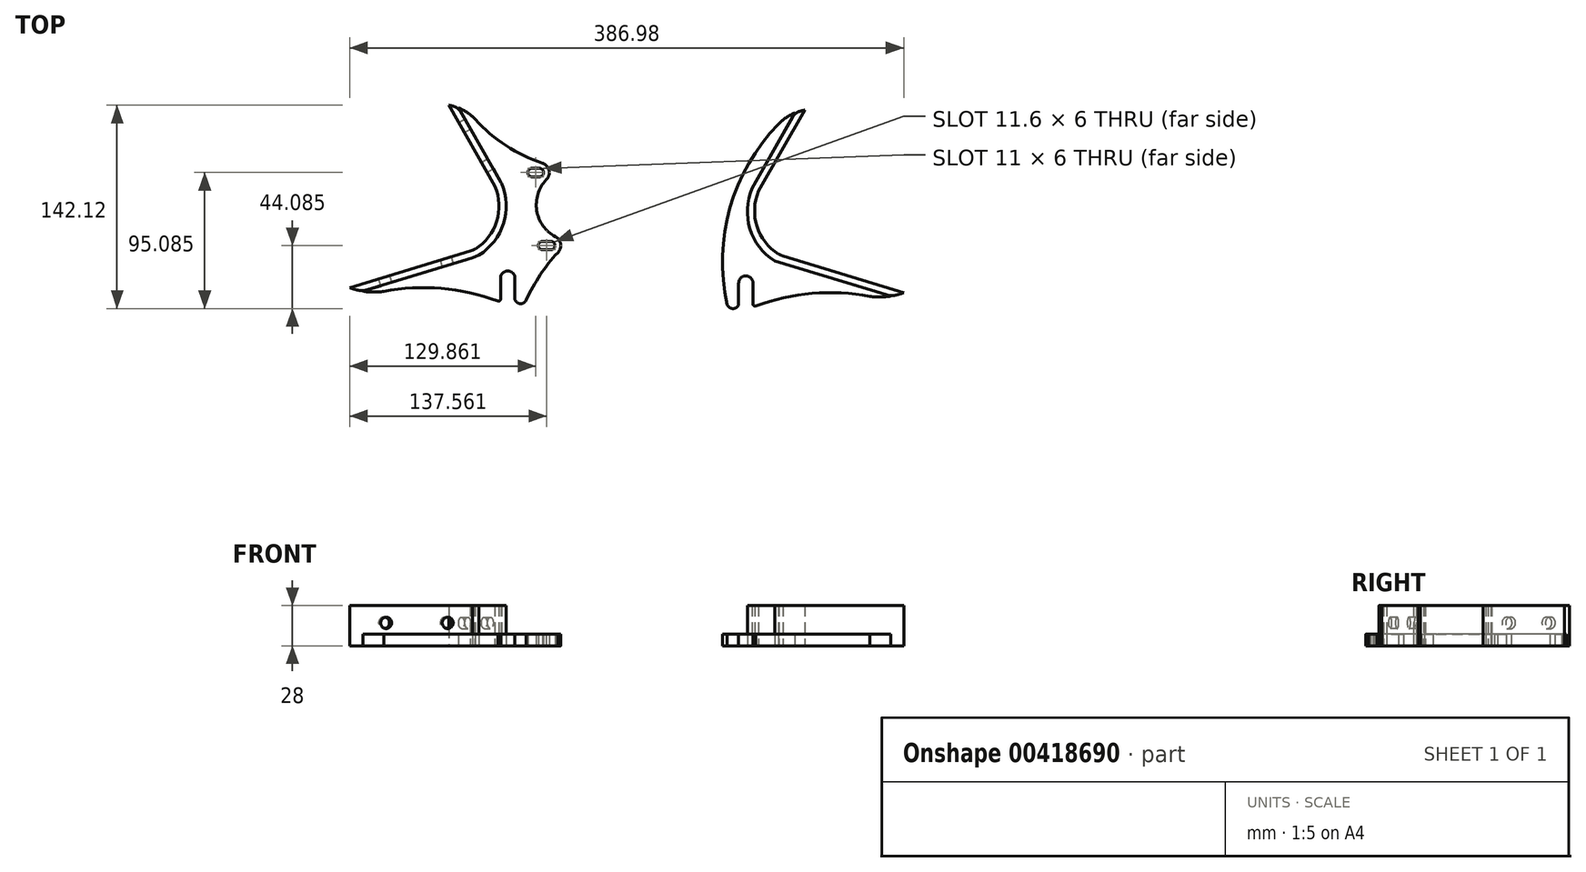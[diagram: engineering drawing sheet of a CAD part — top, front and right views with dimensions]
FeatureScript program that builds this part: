
annotation { "Feature Type Name" : "Feature", "Feature Type Description" : "" }
export const myFeature = defineFeature(function(context is Context, id is Id, definition is map)
    precondition{}
    {
        {
            var Q0;
            Q0=qCreatedBy(makeId("Top.planeOp"),FACE);
            var sketch = newSketch(context, id + "F0", { "sketchPlane" : qUnion([Q0])});
            skArc(sketch, "E0", {"start": v(92.06, 11.01) * mm, "mid": v(90.9, -13.55) * mm, "end": v(105.95, -33) * mm});
            skLineSegment(sketch, "E1", {"start": v(105.95, -33) * mm, "end": v(106.16, -33.11) * mm});
            skLineSegment(sketch, "E2", {"start": v(106.16, -33.11) * mm, "end": v(107.42, -33.6) * mm});
            skLineSegment(sketch, "E3", {"start": v(107.42, -33.6) * mm, "end": v(109.2, -34.29) * mm});
            skLineSegment(sketch, "E4", {"start": v(109.2, -34.29) * mm, "end": v(193.49, -59.91) * mm});
            skArc(sketch, "E5", {"start": v(88.13, -53.19) * mm, "mid": v(83.13, -48.19) * mm, "end": v(78.13, -53.19) * mm});
            skArc(sketch, "E6", {"start": v(88.13, -68.19) * mm, "mid": v(88.92, -69.1) * mm, "end": v(90.13, -69.19) * mm});
            skLineSegment(sketch, "E7", {"start": v(88.13, -53.19) * mm, "end": v(88.13, -68.19) * mm});
            skLineSegment(sketch, "E8", {"start": v(78.13, -53.19) * mm, "end": v(78.13, -68.19) * mm});
            skArc(sketch, "E9", {"start": v(70.13, -68.19) * mm, "mid": v(74.13, -71.06) * mm, "end": v(78.13, -68.19) * mm});
            skArc(sketch, "E10", {"start": v(169.82, -62.54) * mm, "mid": v(129.52, -60.4) * mm, "end": v(90.13, -69.19) * mm});
            skLineSegment(sketch, "E11", {"start": v(124.34, 67.6) * mm, "end": v(92.06, 11.01) * mm});
            skArc(sketch, "E12", {"start": v(105.82, 57.7) * mm, "mid": v(72.04, -0.73) * mm, "end": v(70.13, -68.19) * mm});
            skArc(sketch, "E13", {"start": v(-105.95, -29.54) * mm, "mid": v(-90.9, -10.09) * mm, "end": v(-92.06, 14.47) * mm});
            skLineSegment(sketch, "E14", {"start": v(-105.95, -29.54) * mm, "end": v(-106.16, -29.65) * mm});
            skLineSegment(sketch, "E15", {"start": v(-106.16, -29.65) * mm, "end": v(-107.42, -30.14) * mm});
            skLineSegment(sketch, "E16", {"start": v(-107.42, -30.14) * mm, "end": v(-109.2, -30.83) * mm});
            skLineSegment(sketch, "E17", {"start": v(-109.2, -30.83) * mm, "end": v(-193.49, -56.45) * mm});
            skArc(sketch, "E18", {"start": v(-103.3, -33.77) * mm, "mid": v(-86.14, -11.6) * mm, "end": v(-87.46, 16.42) * mm});
            skLineSegment(sketch, "E19", {"start": v(-107.75, -35.61) * mm, "end": v(-103.3, -33.77) * mm});
            skLineSegment(sketch, "E20", {"start": v(-87.72, 16.95) * mm, "end": v(-87.46, 16.42) * mm});
            skArc(sketch, "E21", {"start": v(-78.13, -49.73) * mm, "mid": v(-83.13, -44.73) * mm, "end": v(-88.13, -49.73) * mm});
            skArc(sketch, "E22", {"start": v(-90.13, -65.73) * mm, "mid": v(-88.92, -65.64) * mm, "end": v(-88.13, -64.73) * mm});
            skLineSegment(sketch, "E23", {"start": v(-88.13, -49.73) * mm, "end": v(-88.13, -64.73) * mm});
            skLineSegment(sketch, "E24", {"start": v(-78.13, -49.73) * mm, "end": v(-78.13, -64.73) * mm});
            skArc(sketch, "E25", {"start": v(-53.13, -29.98) * mm, "mid": v(-50.13, -26.98) * mm, "end": v(-53.13, -23.98) * mm});
            skArc(sketch, "E26", {"start": v(-61.13, 21.02) * mm, "mid": v(-58.13, 24.02) * mm, "end": v(-61.13, 27.02) * mm});
            skArc(sketch, "E27", {"start": v(-105.82, 61.16) * mm, "mid": v(-84.33, 42.8) * mm, "end": v(-58.82, 30.63) * mm});
            skArc(sketch, "E28", {"start": v(-58.73, -23.98) * mm, "mid": v(-60.85, -24.85) * mm, "end": v(-61.73, -26.98) * mm});
            skArc(sketch, "E29", {"start": v(-61.73, -26.98) * mm, "mid": v(-60.85, -29.1) * mm, "end": v(-58.73, -29.98) * mm});
            skLineSegment(sketch, "E30", {"start": v(-58.73, -29.98) * mm, "end": v(-53.13, -29.98) * mm});
            skLineSegment(sketch, "E31", {"start": v(-58.73, -23.98) * mm, "end": v(-53.13, -23.98) * mm});
            skArc(sketch, "E32", {"start": v(-66.13, 27.02) * mm, "mid": v(-68.25, 26.15) * mm, "end": v(-69.13, 24.02) * mm});
            skArc(sketch, "E33", {"start": v(-69.13, 24.02) * mm, "mid": v(-68.25, 21.9) * mm, "end": v(-66.13, 21.02) * mm});
            skLineSegment(sketch, "E34", {"start": v(-66.13, 21.02) * mm, "end": v(-61.13, 21.02) * mm});
            skLineSegment(sketch, "E35", {"start": v(-66.13, 27.02) * mm, "end": v(-61.13, 27.02) * mm});
            skArc(sketch, "E36", {"start": v(-56.34, 18.92) * mm, "mid": v(-62.84, -2.56) * mm, "end": v(-49.8, -20.82) * mm});
            skArc(sketch, "E37", {"start": v(-56.34, 18.92) * mm, "mid": v(-54.31, 25.62) * mm, "end": v(-59.1, 30.72) * mm});
            skArc(sketch, "E38", {"start": v(-48.17, -31.92) * mm, "mid": v(-46.2, -25.95) * mm, "end": v(-49.82, -20.8) * mm});
            skArc(sketch, "E39", {"start": v(-48.17, -31.92) * mm, "mid": v(-60.46, -47.44) * mm, "end": v(-70.13, -64.73) * mm});
            skArc(sketch, "E40", {"start": v(-78.13, -64.73) * mm, "mid": v(-74.13, -67.6) * mm, "end": v(-70.13, -64.73) * mm});
            skArc(sketch, "E41", {"start": v(-90.13, -65.73) * mm, "mid": v(-129.52, -56.93) * mm, "end": v(-169.82, -59.08) * mm});
            skLineSegment(sketch, "E42", {"start": v(-107.75, -35.61) * mm, "end": v(-184.27, -58.87) * mm});
            skLineSegment(sketch, "E43", {"start": v(-117.5, 69.16) * mm, "end": v(-87.72, 16.95) * mm});
            skLineSegment(sketch, "E44", {"start": v(-124.34, 71.06) * mm, "end": v(-92.06, 14.47) * mm});
            skArc(sketch, "E45", {"start": v(-105.82, 61.16) * mm, "mid": v(-111.22, 65.8) * mm, "end": v(-117.5, 69.16) * mm});
            skArc(sketch, "E46", {"start": v(-117.5, 69.16) * mm, "mid": v(-120.87, 70.3) * mm, "end": v(-124.34, 71.06) * mm});
            skArc(sketch, "E47", {"start": v(-193.49, -56.45) * mm, "mid": v(-188.94, -57.88) * mm, "end": v(-184.27, -58.87) * mm});
            skArc(sketch, "E48", {"start": v(-184.27, -58.87) * mm, "mid": v(-177.05, -59.5) * mm, "end": v(-169.82, -59.08) * mm});
            skArc(sketch, "E49", {"start": v(169.82, -62.54) * mm, "mid": v(177.05, -62.97) * mm, "end": v(184.27, -62.34) * mm});
            skArc(sketch, "E50", {"start": v(184.27, -62.34) * mm, "mid": v(188.94, -61.35) * mm, "end": v(193.49, -59.91) * mm});
            skArc(sketch, "E51", {"start": v(124.34, 67.6) * mm, "mid": v(120.87, 66.84) * mm, "end": v(117.5, 65.7) * mm});
            skArc(sketch, "E52", {"start": v(117.5, 65.7) * mm, "mid": v(111.22, 62.34) * mm, "end": v(105.82, 57.7) * mm});
            skLineSegment(sketch, "E53", {"start": v(117.5, 65.7) * mm, "end": v(87.46, 12.96) * mm});
            skArc(sketch, "E54", {"start": v(87.46, 12.96) * mm, "mid": v(86.03, -15.31) * mm, "end": v(103.27, -37.76) * mm});
            skLineSegment(sketch, "E55", {"start": v(103.27, -37.76) * mm, "end": v(184.27, -62.34) * mm});
            skSolve(sketch);
        }
        {
            var Q0;
            Q0=makeQuery(id+"F0.imprint","IMPRINT",FACE,{"disambiguationData":[TD([[makeQuery(id+"F0.imprint","IMPRINT",EDGE,{"derivedFrom":sQuery(id+"F0.wireOp",EDGE,"E18")}),-1.0]])]});
            var Q1;
            Q1=makeQuery(id+"F0.imprint","IMPRINT",FACE,{"disambiguationData":[TD([[makeQuery(id+"F0.imprint","IMPRINT",EDGE,{"derivedFrom":sQuery(id+"F0.wireOp",EDGE,"E5")}),-1.0]])]});
            extrude(context, id + "F1", {"entities" : qUnion([Q0, Q1]), "depth" : 8 * mm});
        }
        {
            var Q0;
            Q0=makeQuery(id+"F0.imprint","IMPRINT",FACE,{"disambiguationData":[TD([[makeQuery(id+"F0.imprint","IMPRINT",EDGE,{"derivedFrom":sQuery(id+"F0.wireOp",EDGE,"E13")}),-1.0]])]});
            var Q1;
            Q1=makeQuery(id+"F0.imprint","IMPRINT",FACE,{"disambiguationData":[TD([[makeQuery(id+"F0.imprint","IMPRINT",EDGE,{"derivedFrom":sQuery(id+"F0.wireOp",EDGE,"E0")}),-1.0]])]});
            extrude(context, id + "F2", {"entities" : qUnion([Q0, Q1]), "depth" : 28 * mm});
        }
        {
            var Q0;
            Q0=makeQuery(id+"F2.opExtrude","SWEPT_FACE",FACE,{"disambiguationData":[OSD([sQuery(id+"F0.wireOp",EDGE,"E42")])]});
            cPlane(context, id + "F3", {"entities" : qUnion([Q0]), "cplaneType" : CPlaneType.OFFSET, "offset" : 0 * mm, "width" : 150 * mm, "height" : 150 * mm});
        }
        {
            var Q0;
            Q0=qCreatedBy(id+"F3.planeOp",FACE);
            var sketch = newSketch(context, id + "F4", { "sketchPlane" : qUnion([Q0])});
            skPoint(sketch, "E56", {"position": v(-131.54, 16) * mm});
            skPoint(sketch, "E57", {"position": v(-176.54, 16) * mm});
            skSolve(sketch);
        }
        {
            var Q0;
            Q0=sQuery(id+"F4.wireOp",VERTEX,"E56");
            var Q1;
            Q1=makeQuery(id+"F2.opExtrude","SWEPT_BODY",BODY,{"disambiguationData":[OSD([sQuery(id+"F0.wireOp",EDGE,"E13"),sQuery(id+"F0.wireOp",EDGE,"E14"),sQuery(id+"F0.wireOp",EDGE,"E15"),sQuery(id+"F0.wireOp",EDGE,"E16"),sQuery(id+"F0.wireOp",EDGE,"E17"),sQuery(id+"F0.wireOp",EDGE,"E18"),sQuery(id+"F0.wireOp",EDGE,"E19"),sQuery(id+"F0.wireOp",EDGE,"E20"),sQuery(id+"F0.wireOp",EDGE,"E42"),sQuery(id+"F0.wireOp",EDGE,"E43"),sQuery(id+"F0.wireOp",EDGE,"E44"),sQuery(id+"F0.wireOp",EDGE,"E46"),sQuery(id+"F0.wireOp",EDGE,"E47")])]});
            hole(context, id + "F5", {"style" : HoleStyle.SIMPLE, "endStyle" : HoleEndStyle.THROUGH, "holeDiameter" : 8 * mm, "isTappedThrough" : true, "tappedDepth" : 12 * mm, "tapClearance" : 3, "locations" : qUnion([Q0]), "scope" : qUnion([Q1])});
        }
        {
            var Q0;
            Q0=sQuery(id+"F4.wireOp",VERTEX,"E57");
            var Q1;
            Q1=makeQuery(id+"F2.opExtrude","SWEPT_BODY",BODY,{"disambiguationData":[OSD([sQuery(id+"F0.wireOp",EDGE,"E13"),sQuery(id+"F0.wireOp",EDGE,"E14"),sQuery(id+"F0.wireOp",EDGE,"E15"),sQuery(id+"F0.wireOp",EDGE,"E16"),sQuery(id+"F0.wireOp",EDGE,"E17"),sQuery(id+"F0.wireOp",EDGE,"E18"),sQuery(id+"F0.wireOp",EDGE,"E19"),sQuery(id+"F0.wireOp",EDGE,"E20"),sQuery(id+"F0.wireOp",EDGE,"E42"),sQuery(id+"F0.wireOp",EDGE,"E43"),sQuery(id+"F0.wireOp",EDGE,"E44"),sQuery(id+"F0.wireOp",EDGE,"E46"),sQuery(id+"F0.wireOp",EDGE,"E47")])]});
            hole(context, id + "F6", {"style" : HoleStyle.SIMPLE, "endStyle" : HoleEndStyle.THROUGH, "holeDiameter" : 8 * mm, "isTappedThrough" : true, "tappedDepth" : 12 * mm, "tapClearance" : 3, "locations" : qUnion([Q0]), "scope" : qUnion([Q1])});
        }
        {
            var Q0;
            Q0=makeQuery(id+"F2.opExtrude","SWEPT_EDGE",EDGE,{"disambiguationData":[OSD([sQuery(id+"F0.wireOp",EDGE,"E42"),sQuery(id+"F0.wireOp",EDGE,"E47"),sQuery(id+"F0.wireOp",EDGE,"E48")])]});
            fillet(context, id + "F7", {"entities" : qUnion([Q0]), "radius" : 13 * mm, "tangentPropagation" : true, "allowEdgeOverflow" : false});
        }
        {
            var Q0;
            Q0=makeQuery(id+"F2.opExtrude","SWEPT_EDGE",EDGE,{"disambiguationData":[OSD([sQuery(id+"F0.wireOp",EDGE,"E43"),sQuery(id+"F0.wireOp",EDGE,"E45"),sQuery(id+"F0.wireOp",EDGE,"E46")])]});
            fillet(context, id + "F8", {"entities" : qUnion([Q0]), "radius" : 9 * mm, "tangentPropagation" : true, "allowEdgeOverflow" : false});
        }
        {
            var Q0;
            Q0=makeQuery(id+"F2.opExtrude","SWEPT_FACE",FACE,{"disambiguationData":[OSD([sQuery(id+"F0.wireOp",EDGE,"E43")])]});
            var sketch = newSketch(context, id + "F9", { "sketchPlane" : qUnion([Q0])});
            skPoint(sketch, "E58", {"position": v(73.34, 16) * mm});
            skPoint(sketch, "E59", {"position": v(105.34, 16) * mm});
            skSolve(sketch);
        }
        {
            var Q0;
            Q0=sQuery(id+"F9.wireOp",VERTEX,"E58");
            var Q1;
            Q1=sQuery(id+"F9.wireOp",VERTEX,"E59");
            var Q2;
            Q2=makeQuery(id+"F2.opExtrude","SWEPT_BODY",BODY,{"disambiguationData":[OSD([sQuery(id+"F0.wireOp",EDGE,"E13"),sQuery(id+"F0.wireOp",EDGE,"E14"),sQuery(id+"F0.wireOp",EDGE,"E15"),sQuery(id+"F0.wireOp",EDGE,"E16"),sQuery(id+"F0.wireOp",EDGE,"E17"),sQuery(id+"F0.wireOp",EDGE,"E18"),sQuery(id+"F0.wireOp",EDGE,"E19"),sQuery(id+"F0.wireOp",EDGE,"E20"),sQuery(id+"F0.wireOp",EDGE,"E42"),sQuery(id+"F0.wireOp",EDGE,"E43"),sQuery(id+"F0.wireOp",EDGE,"E44"),sQuery(id+"F0.wireOp",EDGE,"E46"),sQuery(id+"F0.wireOp",EDGE,"E47")])]});
            hole(context, id + "F10", {"style" : HoleStyle.SIMPLE, "endStyle" : HoleEndStyle.THROUGH, "holeDiameter" : 8 * mm, "majorDiameter" : 5 * mm, "isTappedThrough" : true, "tappedDepth" : 12 * mm, "tapClearance" : 3, "locations" : qUnion([Q0, Q1]), "scope" : qUnion([Q2])});
        }
        {
            var Q0;
            Q0=makeQuery(id+"F2.opExtrude","SWEPT_FACE",FACE,{"disambiguationData":[OSD([sQuery(id+"F0.wireOp",EDGE,"E53")])]});
            cPlane(context, id + "F11", {"entities" : qUnion([Q0]), "cplaneType" : CPlaneType.OFFSET, "offset" : 25 * mm, "width" : 150 * mm, "height" : 150 * mm});
        }
        {
            var Q0;
            Q0=qCreatedBy(id+"F11.planeOp",FACE);
            var sketch = newSketch(context, id + "F12", { "sketchPlane" : qUnion([Q0])});
            skPoint(sketch, "E60", {"position": v(-102.29, 16) * mm});
            skPoint(sketch, "E61", {"position": v(-70.29, 16) * mm});
            skSolve(sketch);
        }
        {
            var Q0;
            Q0=sQuery(id+"F12.wireOp",VERTEX,"E61");
            var Q1;
            Q1=sQuery(id+"F12.wireOp",VERTEX,"E60");
            var Q2;
            Q2=makeQuery(id+"F1.opExtrude","SWEPT_BODY",BODY,{"disambiguationData":[OSD([sQuery(id+"F0.wireOp",EDGE,"E5"),sQuery(id+"F0.wireOp",EDGE,"E6"),sQuery(id+"F0.wireOp",EDGE,"E7"),sQuery(id+"F0.wireOp",EDGE,"E8"),sQuery(id+"F0.wireOp",EDGE,"E9"),sQuery(id+"F0.wireOp",EDGE,"E10"),sQuery(id+"F0.wireOp",EDGE,"E12"),sQuery(id+"F0.wireOp",EDGE,"E49"),sQuery(id+"F0.wireOp",EDGE,"E52"),sQuery(id+"F0.wireOp",EDGE,"E53"),sQuery(id+"F0.wireOp",EDGE,"E54"),sQuery(id+"F0.wireOp",EDGE,"E55")])]});
            hole(context, id + "F13", {"style" : HoleStyle.SIMPLE, "endStyle" : HoleEndStyle.THROUGH, "holeDiameter" : 8 * mm, "majorDiameter" : 5 * mm, "isTappedThrough" : true, "tappedDepth" : 12 * mm, "tapClearance" : 3, "locations" : qUnion([Q0, Q1]), "scope" : qUnion([Q2])});
        }
        {
            var Q0;
            Q0=makeQuery(id+"F2.opExtrude","SWEPT_EDGE",EDGE,{"disambiguationData":[OSD([sQuery(id+"F0.wireOp",EDGE,"E51"),sQuery(id+"F0.wireOp",EDGE,"E52"),sQuery(id+"F0.wireOp",EDGE,"E53")])]});
            fillet(context, id + "F14", {"entities" : qUnion([Q0]), "radius" : 9 * mm, "tangentPropagation" : true, "allowEdgeOverflow" : false});
        }
        {
            var Q0;
            Q0=makeQuery(id+"F2.opExtrude","SWEPT_FACE",FACE,{"disambiguationData":[OSD([sQuery(id+"F0.wireOp",EDGE,"E55")])]});
            var sketch = newSketch(context, id + "F15", { "sketchPlane" : qUnion([Q0])});
            skPoint(sketch, "E62", {"position": v(132.55, 16) * mm});
            skPoint(sketch, "E63", {"position": v(177.55, 16) * mm});
            skSolve(sketch);
        }
        {
            var Q0;
            Q0=sQuery(id+"F15.wireOp",VERTEX,"E62");
            var Q1;
            Q1=sQuery(id+"F15.wireOp",VERTEX,"E63");
            var Q2;
            Q2=makeQuery(id+"F1.opExtrude","SWEPT_BODY",BODY,{"disambiguationData":[OSD([sQuery(id+"F0.wireOp",EDGE,"E5"),sQuery(id+"F0.wireOp",EDGE,"E6"),sQuery(id+"F0.wireOp",EDGE,"E7"),sQuery(id+"F0.wireOp",EDGE,"E8"),sQuery(id+"F0.wireOp",EDGE,"E9"),sQuery(id+"F0.wireOp",EDGE,"E10"),sQuery(id+"F0.wireOp",EDGE,"E12"),sQuery(id+"F0.wireOp",EDGE,"E49"),sQuery(id+"F0.wireOp",EDGE,"E52"),sQuery(id+"F0.wireOp",EDGE,"E53"),sQuery(id+"F0.wireOp",EDGE,"E54"),sQuery(id+"F0.wireOp",EDGE,"E55")])]});
            hole(context, id + "F16", {"style" : HoleStyle.SIMPLE, "endStyle" : HoleEndStyle.THROUGH, "holeDiameter" : 8 * mm, "isTappedThrough" : true, "tappedDepth" : 12 * mm, "tapClearance" : 3, "locations" : qUnion([Q0, Q1]), "scope" : qUnion([Q2])});
        }
        {
            var Q0;
            Q0=makeQuery(id+"F2.opExtrude","SWEPT_EDGE",EDGE,{"disambiguationData":[OSD([sQuery(id+"F0.wireOp",EDGE,"E49"),sQuery(id+"F0.wireOp",EDGE,"E50"),sQuery(id+"F0.wireOp",EDGE,"E55")])]});
            fillet(context, id + "F17", {"entities" : qUnion([Q0]), "radius" : 13 * mm, "tangentPropagation" : true, "allowEdgeOverflow" : false});
        }
    });
